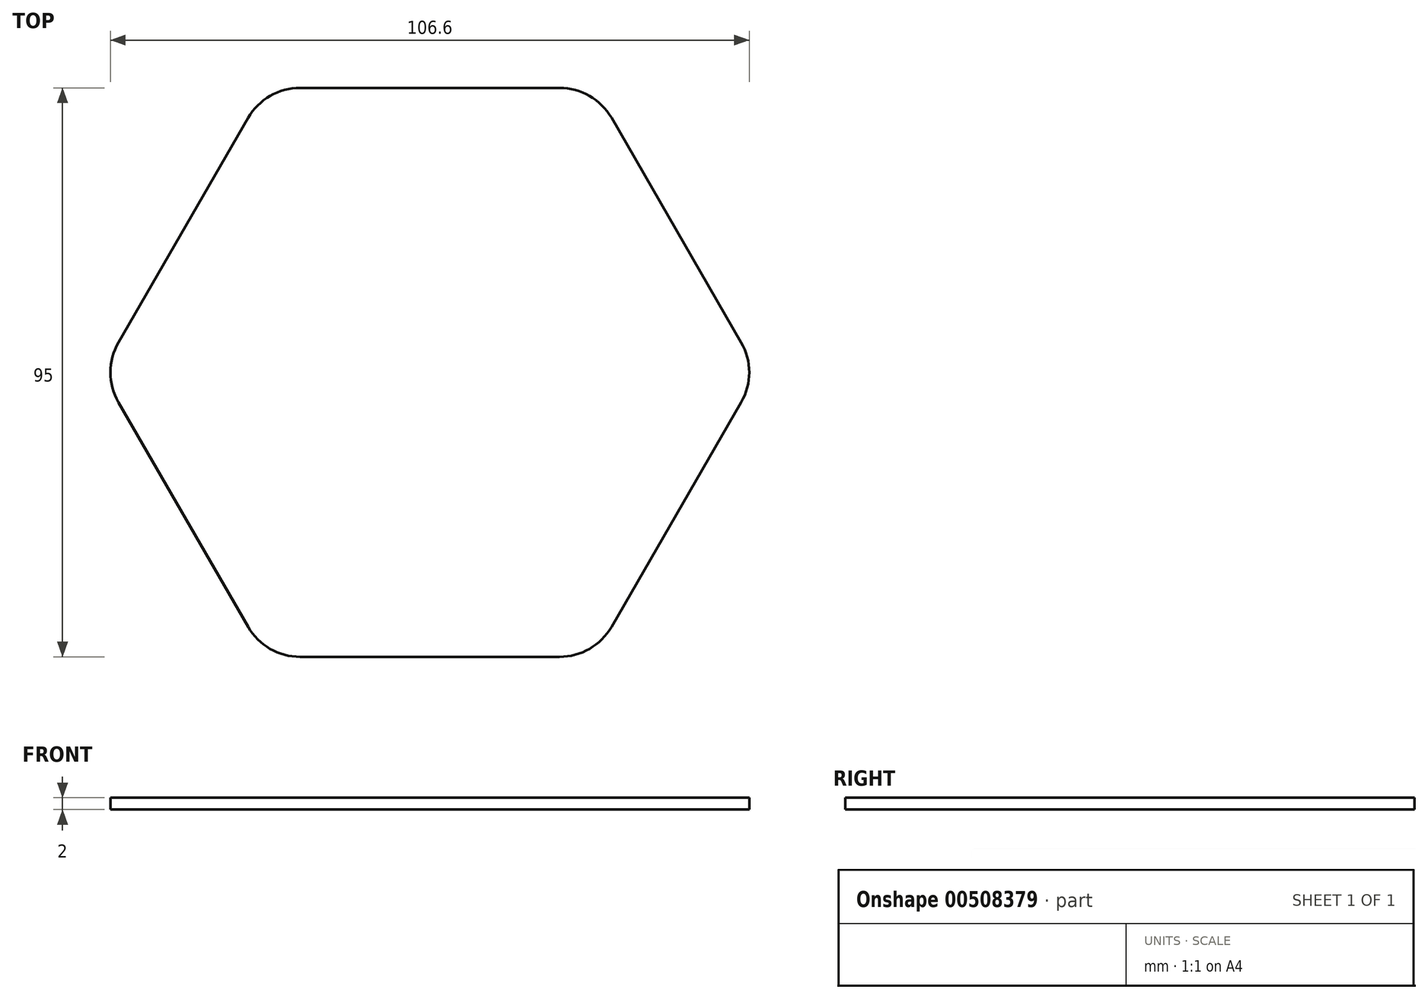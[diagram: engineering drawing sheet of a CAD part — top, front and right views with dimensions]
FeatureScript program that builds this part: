
annotation { "Feature Type Name" : "Feature", "Feature Type Description" : "" }
export const myFeature = defineFeature(function(context is Context, id is Id, definition is map)
    precondition{}
    {
        {
            var Q0;
            Q0=qCreatedBy(makeId("Top.planeOp"),FACE);
            var sketch = newSketch(context, id + "F0", { "sketchPlane" : qUnion([Q0])});
            skCircle(sketch, "E0.cCircle", {"center": v(0, 0) * mm, "radius": 54.85 * mm, "construction": true});
            skLineSegment(sketch, "E0.0", {"start": v(51.96, -5) * mm, "end": v(30.31, -42.5) * mm});
            skLineSegment(sketch, "E0.1", {"start": v(21.65, -47.5) * mm, "end": v(-21.65, -47.5) * mm});
            skLineSegment(sketch, "E0.2", {"start": v(-30.31, -42.5) * mm, "end": v(-51.96, -5) * mm});
            skLineSegment(sketch, "E0.3", {"start": v(-51.96, 5) * mm, "end": v(-30.31, 42.5) * mm});
            skLineSegment(sketch, "E0.4", {"start": v(-21.65, 47.5) * mm, "end": v(21.65, 47.5) * mm});
            skLineSegment(sketch, "E0.5", {"start": v(30.31, 42.5) * mm, "end": v(51.96, 5) * mm});
            skPoint(sketch, "E1.visualSharp", {"position": v(27.42, 47.5) * mm});
            skArc(sketch, "E1.filletArc", {"start": v(30.31, 42.5) * mm, "mid": v(26.65, 46.16) * mm, "end": v(21.65, 47.5) * mm});
            skPoint(sketch, "E2.visualSharp", {"position": v(-27.42, 47.5) * mm});
            skArc(sketch, "E2.filletArc", {"start": v(-21.65, 47.5) * mm, "mid": v(-26.65, 46.16) * mm, "end": v(-30.31, 42.5) * mm});
            skPoint(sketch, "E3.visualSharp", {"position": v(-54.85, 0) * mm});
            skArc(sketch, "E3.filletArc", {"start": v(-51.96, 5) * mm, "mid": v(-53.3, 0) * mm, "end": v(-51.96, -5) * mm});
            skPoint(sketch, "E4.visualSharp", {"position": v(-27.42, -47.5) * mm});
            skArc(sketch, "E4.filletArc", {"start": v(-30.31, -42.5) * mm, "mid": v(-26.65, -46.16) * mm, "end": v(-21.65, -47.5) * mm});
            skPoint(sketch, "E5.visualSharp", {"position": v(27.42, -47.5) * mm});
            skArc(sketch, "E5.filletArc", {"start": v(21.65, -47.5) * mm, "mid": v(26.65, -46.16) * mm, "end": v(30.31, -42.5) * mm});
            skPoint(sketch, "E6.visualSharp", {"position": v(54.85, 0) * mm});
            skArc(sketch, "E6.filletArc", {"start": v(51.96, -5) * mm, "mid": v(53.3, 0) * mm, "end": v(51.96, 5) * mm});
            skSolve(sketch);
        }
        {
            var Q0;
            Q0=makeQuery(id+"F0.imprint","IMPRINT",FACE,{"disambiguationData":[TD([[makeQuery(id+"F0.imprint","IMPRINT",EDGE,{"derivedFrom":sQuery(id+"F0.wireOp",EDGE,"E0.0")}),-1.0]])]});
            extrude(context, id + "F1", {"entities" : qUnion([Q0]), "depth" : 2 * mm});
        }
    });
